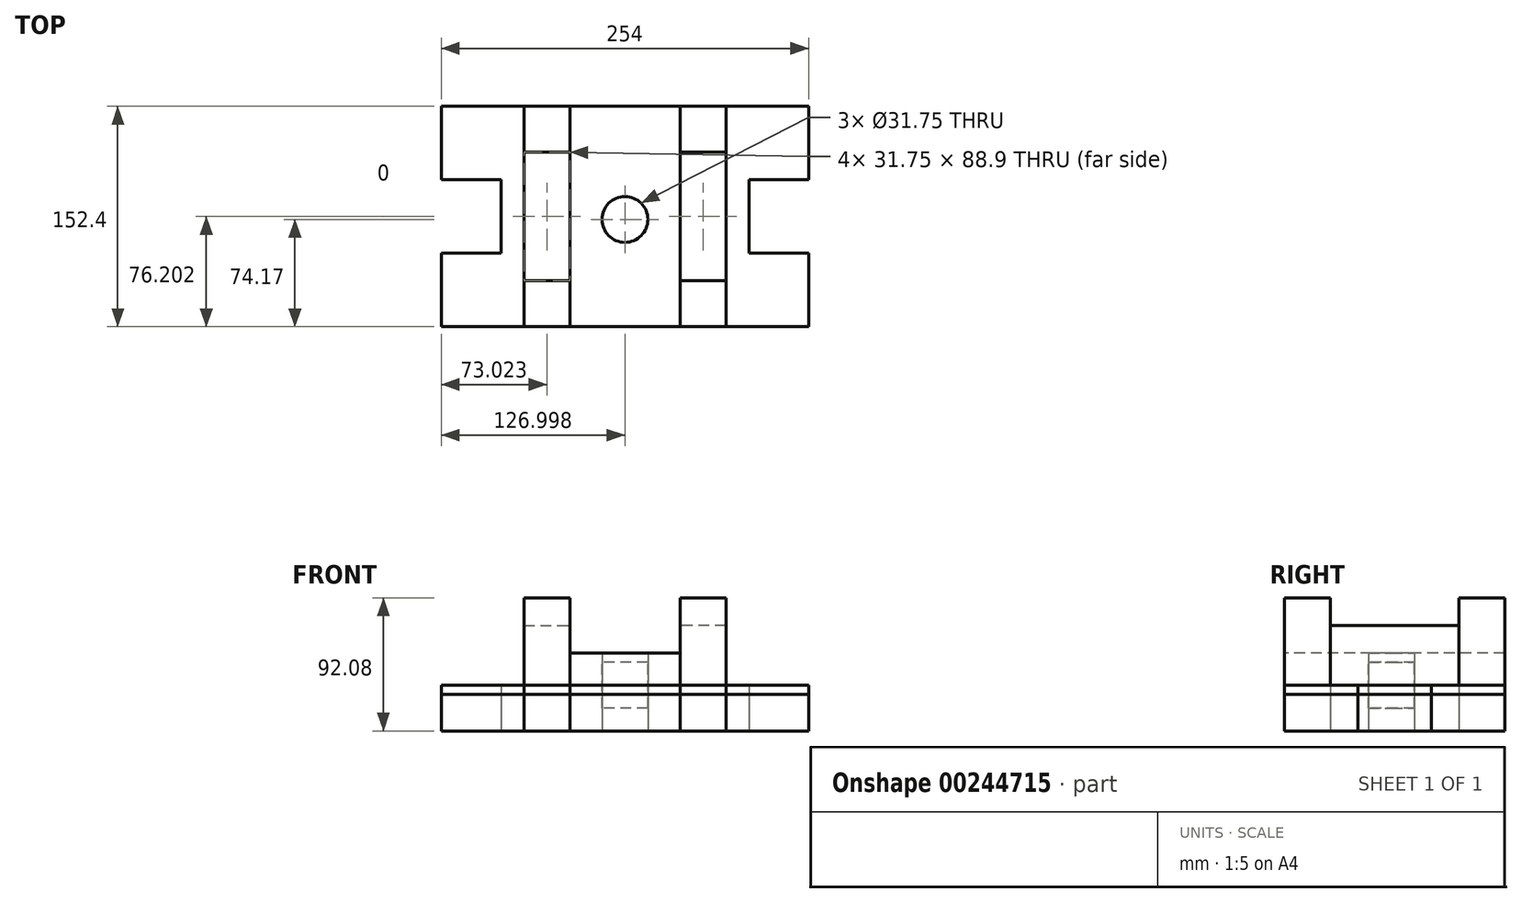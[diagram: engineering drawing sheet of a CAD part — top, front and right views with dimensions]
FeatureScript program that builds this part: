
annotation { "Feature Type Name" : "Feature", "Feature Type Description" : "" }
export const myFeature = defineFeature(function(context is Context, id is Id, definition is map)
    precondition{}
    {
        {
            var Q0;
            Q0=qCreatedBy(makeId("Top.planeOp"),FACE);
            var sketch = newSketch(context, id + "F0", { "sketchPlane" : qUnion([Q0])});
            skLineSegment(sketch, "E0", {"start": v(-128.95, 78.23) * mm, "end": v(-71.8, 78.23) * mm});
            skLineSegment(sketch, "E1", {"start": v(125.05, 78.23) * mm, "end": v(125.05, 27.43) * mm});
            skLineSegment(sketch, "E2", {"start": v(-128.95, 78.23) * mm, "end": v(-128.95, 27.43) * mm});
            skLineSegment(sketch, "E3", {"start": v(-128.95, -74.17) * mm, "end": v(-71.8, -74.17) * mm});
            skLineSegment(sketch, "E4", {"start": v(125.05, 27.43) * mm, "end": v(83.77, 27.43) * mm});
            skLineSegment(sketch, "E5", {"start": v(83.77, 27.43) * mm, "end": v(83.77, -23.37) * mm});
            skLineSegment(sketch, "E6", {"start": v(125.05, -23.37) * mm, "end": v(83.77, -23.37) * mm});
            skLineSegment(sketch, "E7.trimOffspring", {"start": v(125.05, -23.37) * mm, "end": v(125.05, -74.17) * mm});
            skLineSegment(sketch, "E8", {"start": v(-128.95, 27.43) * mm, "end": v(-87.68, 27.43) * mm});
            skLineSegment(sketch, "E9", {"start": v(-87.68, 27.43) * mm, "end": v(-87.68, -23.37) * mm});
            skLineSegment(sketch, "E10", {"start": v(-87.68, -23.37) * mm, "end": v(-128.95, -23.37) * mm});
            skLineSegment(sketch, "E11.trimOffspring", {"start": v(-128.95, -23.37) * mm, "end": v(-128.95, -74.17) * mm});
            skLineSegment(sketch, "E12.trimOffspring", {"start": v(67.9, 78.23) * mm, "end": v(125.05, 78.23) * mm});
            skLineSegment(sketch, "E13.trimOffspring", {"start": v(67.9, -74.17) * mm, "end": v(125.05, -74.17) * mm});
            skLineSegment(sketch, "E14", {"start": v(-71.8, 78.23) * mm, "end": v(-40.05, 78.23) * mm});
            skLineSegment(sketch, "E15", {"start": v(-71.8, -74.17) * mm, "end": v(-40.05, -74.17) * mm});
            skLineSegment(sketch, "E16", {"start": v(-40.05, -74.17) * mm, "end": v(-40.05, 78.23) * mm});
            skLineSegment(sketch, "E17", {"start": v(67.9, 78.23) * mm, "end": v(36.15, 78.23) * mm});
            skLineSegment(sketch, "E18", {"start": v(36.15, 78.23) * mm, "end": v(36.15, 0) * mm});
            skLineSegment(sketch, "E19", {"start": v(36.15, -74.17) * mm, "end": v(67.9, -74.17) * mm});
            skLineSegment(sketch, "E20", {"start": v(-1.95, -74.17) * mm, "end": v(36.15, -74.17) * mm});
            skLineSegment(sketch, "E21", {"start": v(-1.95, 78.23) * mm, "end": v(36.15, 78.23) * mm});
            skLineSegment(sketch, "E22", {"start": v(36.15, -74.17) * mm, "end": v(36.15, 0) * mm});
            skCircle(sketch, "E23", {"center": v(-1.95, 0) * mm, "radius": 15.88 * mm});
            skPoint(sketch, "E24.start.orphan", {"position": v(-40.05, 0) * mm});
            skLineSegment(sketch, "E25", {"start": v(-40.05, 78.23) * mm, "end": v(-1.95, 78.23) * mm});
            skLineSegment(sketch, "E26", {"start": v(-1.95, -74.17) * mm, "end": v(-40.05, -74.17) * mm});
            skLineSegment(sketch, "E27", {"start": v(67.9, 78.23) * mm, "end": v(67.9, 46.48) * mm});
            skLineSegment(sketch, "E28", {"start": v(67.9, 46.48) * mm, "end": v(36.15, 46.48) * mm});
            skLineSegment(sketch, "E29", {"start": v(67.9, -74.17) * mm, "end": v(67.9, -42.42) * mm});
            skLineSegment(sketch, "E30", {"start": v(67.9, -42.42) * mm, "end": v(36.15, -42.42) * mm});
            skLineSegment(sketch, "E31", {"start": v(67.9, 46.48) * mm, "end": v(67.9, -42.42) * mm});
            skLineSegment(sketch, "E32", {"start": v(-71.8, 78.23) * mm, "end": v(-71.8, 46.48) * mm});
            skLineSegment(sketch, "E33", {"start": v(-71.8, 46.48) * mm, "end": v(-40.05, 46.48) * mm});
            skLineSegment(sketch, "E34", {"start": v(-71.8, -74.17) * mm, "end": v(-71.8, -42.42) * mm});
            skLineSegment(sketch, "E35", {"start": v(-71.8, -42.42) * mm, "end": v(-40.05, -42.42) * mm});
            skLineSegment(sketch, "E36", {"start": v(-71.8, 46.48) * mm, "end": v(-71.8, -42.42) * mm});
            skSolve(sketch);
        }
        {
            var Q0;
            Q0=makeQuery(id+"F0.imprint","IMPRINT",FACE,{"disambiguationData":[TD([[makeQuery(id+"F0.imprint","IMPRINT",EDGE,{"derivedFrom":sQuery(id+"F0.wireOp",EDGE,"E16")}),-1.0]])]});
            var sketch = newSketch(context, id + "F1", { "sketchPlane" : qUnion([Q0])});
            skSolve(sketch);
        }
        {
            var Q0;
            {var subQ0=sQuery(id+"F0.wireOp",EDGE,"E15");Q0=makeQuery(id+"F0.imprint","IMPRINT",FACE,{"disambiguationData":[TD([[makeQuery(id+"F0.imprint","IMPRINT",EDGE,{"derivedFrom":subQ0}),1.0]])]});}
            var Q1;
            {var subQ0=sQuery(id+"F0.wireOp",EDGE,"E17");Q1=makeQuery(id+"F0.imprint","IMPRINT",FACE,{"disambiguationData":[TD([[makeQuery(id+"F0.imprint","IMPRINT",EDGE,{"derivedFrom":subQ0}),1.0]])]});}
            var Q2;
            {var subQ0=sQuery(id+"F0.wireOp",EDGE,"E19");Q2=makeQuery(id+"F0.imprint","IMPRINT",FACE,{"disambiguationData":[TD([[makeQuery(id+"F0.imprint","IMPRINT",EDGE,{"derivedFrom":subQ0}),1.0]])]});}
            var Q3;
            {var subQ0=sQuery(id+"F0.wireOp",EDGE,"E14");Q3=makeQuery(id+"F0.imprint","IMPRINT",FACE,{"disambiguationData":[TD([[makeQuery(id+"F0.imprint","IMPRINT",EDGE,{"derivedFrom":subQ0}),-1.0]])]});}
            extrude(context, id + "F2", {"entities" : qUnion([Q0, Q1, Q2, Q3]), "depth" : 92.07 * mm});
        }
        {
            var Q0;
            {var subQ4=sQuery(id+"F0.wireOp",EDGE,"E20");Q0=makeQuery(id+"F1.imprint","IMPRINT",FACE,{"disambiguationData":[TD([[makeQuery(id+"F1.imprint","IMPRINT",EDGE,{"derivedFrom":makeQuery(id+"F0.imprint","IMPRINT",EDGE,{"derivedFrom":subQ4})}),1.0]])]});}
            extrude(context, id + "F3", {"entities" : qUnion([Q0]), "depth" : 53.97 * mm});
        }
        {
            var Q0;
            Q0 = qSketchRegion(id + "F0", true);
            extrude(context, id + "F4", {"entities" : qUnion([Q0]), "depth" : 31.75 * mm});
        }
        {
            var Q0;
            Q0 = qSketchRegion(id + "F0", true);
            extrude(context, id + "F5", {"entities" : qUnion([Q0]), "depth" : 25.4 * mm});
        }
        {
            var Q0;
            {var subQ0=sQuery(id+"F0.wireOp",EDGE,"E33");Q0=makeQuery(id+"F0.imprint","IMPRINT",FACE,{"disambiguationData":[TD([[makeQuery(id+"F0.imprint","IMPRINT",EDGE,{"derivedFrom":subQ0}),-1.0]])]});}
            var Q1;
            {var subQ1=sQuery(id+"F0.wireOp",EDGE,"E28");Q1=makeQuery(id+"F0.imprint","IMPRINT",FACE,{"disambiguationData":[TD([[makeQuery(id+"F0.imprint","IMPRINT",EDGE,{"derivedFrom":subQ1}),1.0]])]});}
            extrude(context, id + "F6", {"entities" : qUnion([Q0, Q1]), "depth" : 73.02 * mm});
        }
        {
            var Q0;
            Q0=makeQuery(id+"F0.imprint","IMPRINT",FACE,{"disambiguationData":[TD([[makeQuery(id+"F0.imprint","IMPRINT",EDGE,{"derivedFrom":sQuery(id+"F0.wireOp",EDGE,"E23")}),1.0]])]});
            extrude(context, id + "F7", {"entities" : qUnion([Q0]), "depth" : 47.62 * mm});
        }
        {
            var Q0;
            Q0=makeQuery(id+"F7.opExtrude","CAP_FACE",FACE,{"disambiguationData":[OSD([sQuery(id+"F0.wireOp",EDGE,"E23")])],"isStart":false});
            extrude(context, id + "F8", {"entities" : qUnion([Q0]), "oppositeDirection" : true, "depth" : 31.75 * mm});
        }
    });
